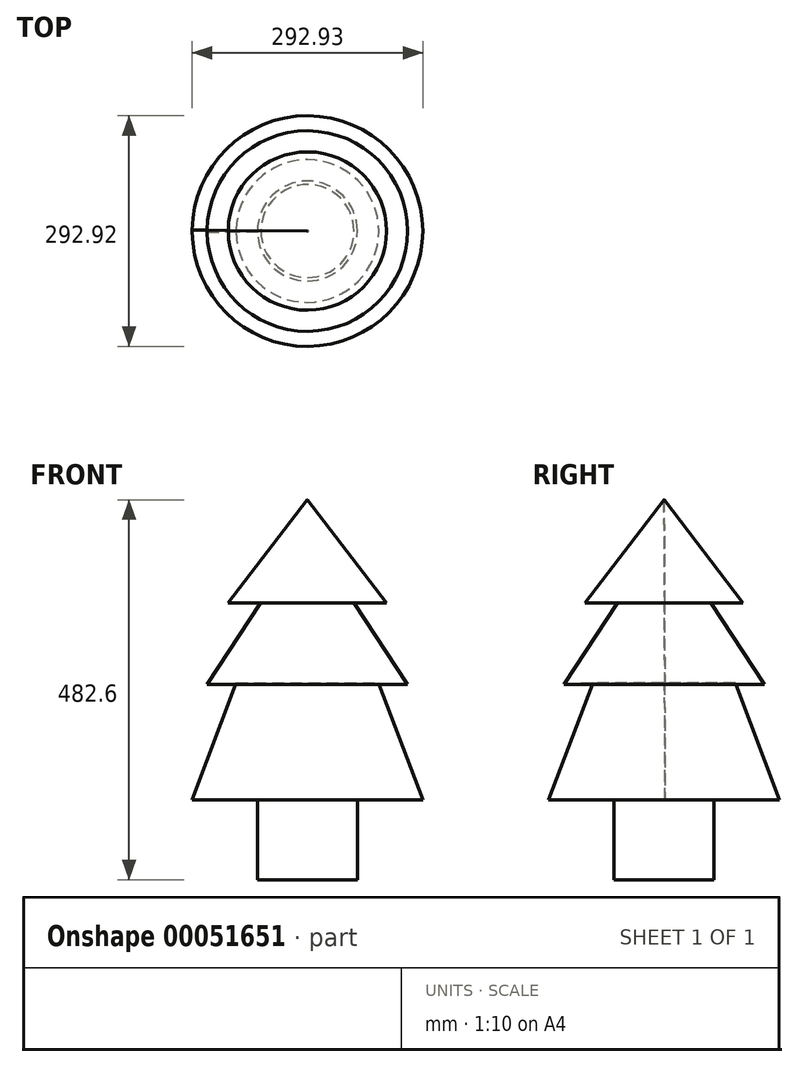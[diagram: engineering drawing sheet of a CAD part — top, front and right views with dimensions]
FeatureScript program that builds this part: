
annotation { "Feature Type Name" : "Feature", "Feature Type Description" : "" }
export const myFeature = defineFeature(function(context is Context, id is Id, definition is map)
    precondition{}
    {
        {
            var Q0;
            Q0=qCreatedBy(makeId("Top.planeOp"),FACE);
            var sketch = newSketch(context, id + "F0", { "sketchPlane" : qUnion([Q0])});
            skCircle(sketch, "E0", {"center": v(0, 0) * mm, "radius": 152.4 * mm});
            skSolve(sketch);
        }
        {
            var Q0;
            Q0 = qSketchRegion(id + "F0", true);
            extrude(context, id + "F6", {"entities" : qUnion([Q0]), "endBound" : BoundingType.SYMMETRIC, "depth" : 381 * mm});
        }
        {
            var Q0;
            Q0=qCreatedBy(makeId("Front.planeOp"),FACE);
            var sketch = newSketch(context, id + "F1", { "sketchPlane" : qUnion([Q0])});
            skLineSegment(sketch, "E1", {"start": v(0, 189.94) * mm, "end": v(0, -190.83) * mm});
            skSolve(sketch);
        }
        {
            var Q0;
            Q0=qCreatedBy(makeId("Front.planeOp"),FACE);
            var sketch = newSketch(context, id + "F2", { "sketchPlane" : qUnion([Q0])});
            skLineSegment(sketch, "E2", {"start": v(0, 190.9) * mm, "end": v(100.56, 59.26) * mm});
            skLineSegment(sketch, "E3", {"start": v(100.56, 59.26) * mm, "end": v(59.03, 59.9) * mm});
            skLineSegment(sketch, "E4", {"start": v(59.03, 59.9) * mm, "end": v(127.37, -43.7) * mm});
            skLineSegment(sketch, "E5", {"start": v(127.37, -43.7) * mm, "end": v(90.64, -42.25) * mm});
            skLineSegment(sketch, "E6", {"start": v(90.64, -42.25) * mm, "end": v(148.92, -197.04) * mm});
            skLineSegment(sketch, "E7", {"start": v(148.92, -197.04) * mm, "end": v(164.9, -197.04) * mm});
            skLineSegment(sketch, "E8", {"start": v(164.9, -197.04) * mm, "end": v(165.04, 198.99) * mm});
            skLineSegment(sketch, "E9", {"start": v(165.04, 198.99) * mm, "end": v(0, 190.9) * mm});
            skSolve(sketch);
        }
        {
            var Q0;
            Q0 = qSketchRegion(id + "F2", true);
            var Q1;
            Q1=sQuery(id+"F1.wireOp",EDGE,"E1");
            revolve(context, id + "F3", {"operationType" : NewBodyOperationType.REMOVE, "entities" : qUnion([Q0]), "axis" : qUnion([Q1]), "revolveType" : RevolveType.SYMMETRIC, "angle" : 359 * degree});
        }
        {
            var Q0;
            Q0=makeQuery(id+"F3.boolean.opBoolean","COPY",FACE,{"derivedFrom":makeQuery(id+"F3.opRevolve","CAP_FACE",FACE,{"disambiguationData":[OSD([sQuery(id+"F2.wireOp",EDGE,"E2"),sQuery(id+"F2.wireOp",EDGE,"E3"),sQuery(id+"F2.wireOp",EDGE,"E4"),sQuery(id+"F2.wireOp",EDGE,"E5"),sQuery(id+"F2.wireOp",EDGE,"E6"),sQuery(id+"F2.wireOp",EDGE,"E7"),sQuery(id+"F2.wireOp",EDGE,"E8"),sQuery(id+"F2.wireOp",EDGE,"E9")])],"isStart":false})});
            var sketch = newSketch(context, id + "F7", { "sketchPlane" : qUnion([Q0])});
            skLineSegment(sketch, "E10", {"start": v(-0.3, 190.5) * mm, "end": v(-100.56, 59.26) * mm});
            skLineSegment(sketch, "E11", {"start": v(-59.03, 59.9) * mm, "end": v(-127.37, -43.7) * mm});
            skLineSegment(sketch, "E12", {"start": v(-100.56, 59.26) * mm, "end": v(-59.03, 59.26) * mm});
            skLineSegment(sketch, "E13", {"start": v(-59.03, 59.26) * mm, "end": v(-127.37, -43.7) * mm});
            skLineSegment(sketch, "E14", {"start": v(-127.37, -43.7) * mm, "end": v(-90.64, -43.7) * mm});
            skLineSegment(sketch, "E15", {"start": v(-90.64, -43.7) * mm, "end": v(-145.9, -190.5) * mm});
            skLineSegment(sketch, "E16", {"start": v(-145.9, -190.5) * mm, "end": v(-152.4, -190.5) * mm});
            skLineSegment(sketch, "E17", {"start": v(-152.4, 190.5) * mm, "end": v(-0.3, 190.5) * mm});
            skSolve(sketch);
        }
        {
            var Q0;
            {var subQ1=sQuery(id+"F7.wireOp",EDGE,"E10");Q0=makeQuery(id+"F7.imprint","IMPRINT",FACE,{"disambiguationData":[TD([[makeQuery(id+"F7.imprint","IMPRINT",EDGE,{"derivedFrom":subQ1}),-1.0]])]});}
            extrude(context, id + "F8", {"entities" : qUnion([Q0]), "operationType" : NewBodyOperationType.REMOVE, "oppositeDirection" : true, "depth" : 25.4 * mm});
        }
        {
            var Q0;
            Q0=makeQuery(id+"F6.opExtrude","CAP_FACE",FACE,{"disambiguationData":[OSD([sQuery(id+"F0.wireOp",EDGE,"E0")])],"isStart":true});
            var sketch = newSketch(context, id + "F4", { "sketchPlane" : qUnion([Q0])});
            skCircle(sketch, "E18", {"center": v(0, 0) * mm, "radius": 63.5 * mm});
            skSolve(sketch);
        }
        {
            var Q0;
            Q0 = qSketchRegion(id + "F4", true);
            extrude(context, id + "F5", {"entities" : qUnion([Q0]), "operationType" : NewBodyOperationType.ADD, "depth" : 101.6 * mm});
        }
    });
